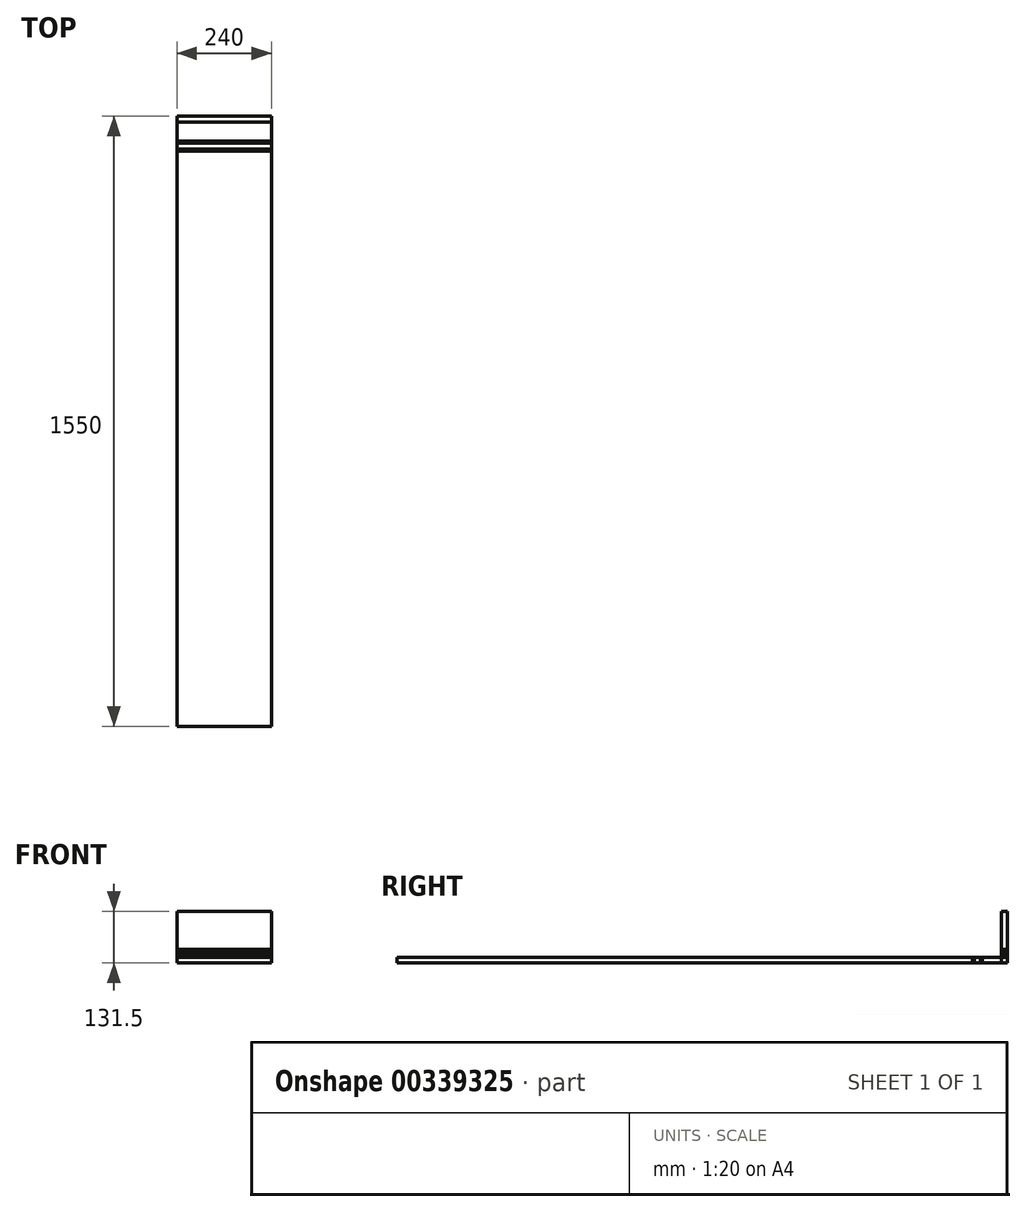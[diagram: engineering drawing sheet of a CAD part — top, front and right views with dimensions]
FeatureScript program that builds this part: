
annotation { "Feature Type Name" : "Feature", "Feature Type Description" : "" }
export const myFeature = defineFeature(function(context is Context, id is Id, definition is map)
    precondition{}
    {
        {
            assignVariable(context, id + "F0", {"name" : "thickness", "anyValue" : 1.5});
        }
        {
            var Q0;
            Q0=qCreatedBy(makeId("Top.planeOp"),FACE);
            var sketch = newSketch(context, id + "F1", { "sketchPlane" : qUnion([Q0])});
            skLineSegment(sketch, "E0.bottom", {"start": v(0, 0) * mm, "end": v(240, 0) * mm});
            skLineSegment(sketch, "E0.top", {"start": v(0, -15) * mm, "end": v(240, -15) * mm});
            skLineSegment(sketch, "E0.left", {"start": v(0, 0) * mm, "end": v(0, -15) * mm});
            skLineSegment(sketch, "E0.right", {"start": v(240, 0) * mm, "end": v(240, -15) * mm});
            skSolve(sketch);
        }
        {
            var Q0;
            Q0 = qSketchRegion(id + "F1", true);
            extrude(context, id + "F2", {"entities" : qUnion([Q0]), "depth" : (133 - getVariable(context, 'thickness')) * mm});
        }
        {
            var Q0;
            Q0=qCreatedBy(makeId("Front.planeOp"),FACE);
            var sketch = newSketch(context, id + "F3", { "sketchPlane" : qUnion([Q0])});
            skLineSegment(sketch, "E1.bottom", {"start": v(0, 0) * mm, "end": v(240, 0) * mm});
            skLineSegment(sketch, "E1.top", {"start": v(0, 15) * mm, "end": v(240, 15) * mm});
            skLineSegment(sketch, "E1.left", {"start": v(0, 0) * mm, "end": v(0, 15) * mm});
            skLineSegment(sketch, "E1.right", {"start": v(240, 0) * mm, "end": v(240, 15) * mm});
            skSolve(sketch);
        }
        {
            var Q0;
            Q0 = qSketchRegion(id + "F3", true);
            extrude(context, id + "F4", {"entities" : qUnion([Q0]), "depth" : (65 - getVariable(context, 'thickness')) * mm});
        }
        {
            var Q0;
            Q0 = qSketchRegion(id + "F3", true);
            extrude(context, id + "F5", {"entities" : qUnion([Q0]), "depth" : (70 - getVariable(context, 'thickness')) * mm});
        }
        {
            var Q0;
            Q0 = qSketchRegion(id + "F3", true);
            extrude(context, id + "F6", {"entities" : qUnion([Q0]), "depth" : (85 - getVariable(context, 'thickness')) * mm});
        }
        {
            var Q0;
            Q0 = qSketchRegion(id + "F3", true);
            extrude(context, id + "F7", {"entities" : qUnion([Q0]), "depth" : (90 - getVariable(context, 'thickness')) * mm});
        }
        {
            var Q0;
            Q0 = qSketchRegion(id + "F3", true);
            extrude(context, id + "F8", {"entities" : qUnion([Q0]), "depth" : 1550 * mm});
        }
        {
            var Q0;
            Q0 = qSketchRegion(id + "F1", true);
            extrude(context, id + "F9", {"entities" : qUnion([Q0]), "depth" : (20 - getVariable(context, 'thickness')) * mm});
        }
        {
            var Q0;
            Q0 = qSketchRegion(id + "F1", true);
            extrude(context, id + "F10", {"entities" : qUnion([Q0]), "depth" : (27 - getVariable(context, 'thickness')) * mm});
        }
        {
            var Q0;
            Q0 = qSketchRegion(id + "F1", true);
            extrude(context, id + "F11", {"entities" : qUnion([Q0]), "depth" : (38 - getVariable(context, 'thickness') * 2) * mm});
        }
    });
